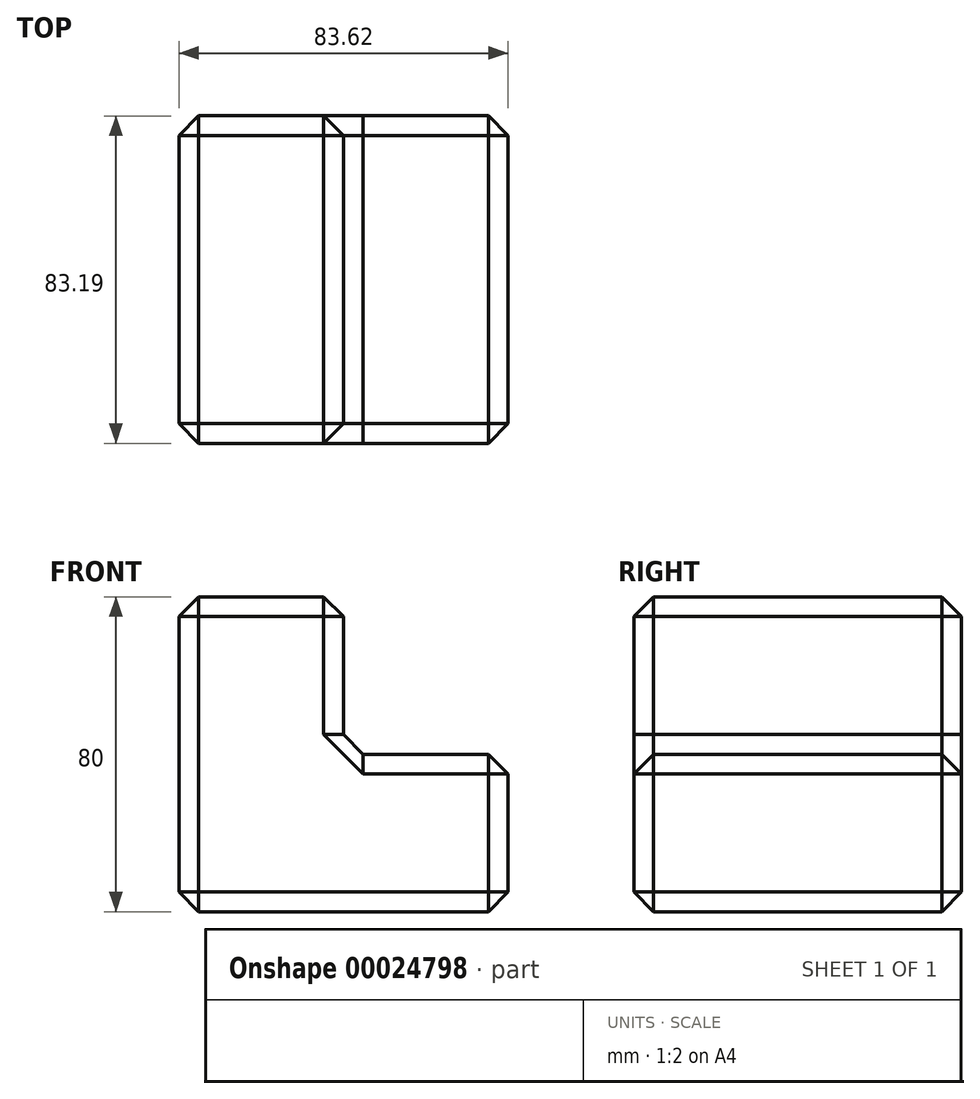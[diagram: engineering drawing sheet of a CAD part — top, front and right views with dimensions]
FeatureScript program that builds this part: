
annotation { "Feature Type Name" : "Feature", "Feature Type Description" : "" }
export const myFeature = defineFeature(function(context is Context, id is Id, definition is map)
    precondition{}
    {
        {
            var Q0;
            Q0=qCreatedBy(makeId("Top.planeOp"),FACE);
            var sketch = newSketch(context, id + "F0", { "sketchPlane" : qUnion([Q0])});
            skLineSegment(sketch, "E0.bottom", {"start": v(-59.13, -45.93) * mm, "end": v(24.5, -45.93) * mm});
            skLineSegment(sketch, "E0.top", {"start": v(-59.13, 37.26) * mm, "end": v(24.5, 37.26) * mm});
            skLineSegment(sketch, "E0.left", {"start": v(-59.13, -45.93) * mm, "end": v(-59.13, 37.26) * mm});
            skLineSegment(sketch, "E0.right", {"start": v(24.5, -45.93) * mm, "end": v(24.5, 37.26) * mm});
            skSolve(sketch);
        }
        {
            var Q0;
            Q0=makeQuery(id+"F0.imprint","IMPRINT",FACE,{"disambiguationData":[TD([[makeQuery(id+"F0.imprint","IMPRINT",EDGE,{"derivedFrom":sQuery(id+"F0.wireOp",EDGE,"E0.bottom")}),1.0]])]});
            extrude(context, id + "F1", {"entities" : qUnion([Q0]), "depth" : 40 * mm});
        }
        {
            var Q0;
            Q0=makeQuery(id+"F1.opExtrude","CAP_FACE",FACE,{"disambiguationData":[OSD([sQuery(id+"F0.wireOp",EDGE,"E0.bottom"),sQuery(id+"F0.wireOp",EDGE,"E0.top"),sQuery(id+"F0.wireOp",EDGE,"E0.left"),sQuery(id+"F0.wireOp",EDGE,"E0.right")])],"isStart":false});
            var sketch = newSketch(context, id + "F2", { "sketchPlane" : qUnion([Q0])});
            skLineSegment(sketch, "E1", {"start": v(-17.32, 37.26) * mm, "end": v(-17.32, -45.93) * mm});
            skSolve(sketch);
        }
        {
            var Q0;
            {var subQ1=sQuery(id+"F2.wireOp",EDGE,"E1");Q0=makeQuery(id+"F2.imprint","IMPRINT",FACE,{"disambiguationData":[TD([[makeQuery(id+"F2.imprint","IMPRINT",EDGE,{"derivedFrom":subQ1}),-1.0]])]});}
            extrude(context, id + "F3", {"entities" : qUnion([Q0]), "operationType" : NewBodyOperationType.ADD, "depth" : 40 * mm});
        }
        {
            var Q0;
            Q0=makeQuery(id+"F3.opExtrude","CAP_FACE",FACE,{"disambiguationData":[OSD([sQuery(id+"F0.wireOp",EDGE,"E0.bottom"),sQuery(id+"F0.wireOp",EDGE,"E0.top"),sQuery(id+"F0.wireOp",EDGE,"E0.left"),sQuery(id+"F2.wireOp",EDGE,"E1")])],"isStart":false});
            var Q1;
            Q1=makeQuery(id+"F3.opExtrude","SWEPT_FACE",FACE,{"disambiguationData":[OSD([sQuery(id+"F2.wireOp",EDGE,"E1")])]});
            var Q2;
            Q2=makeQuery(id+"F1.opExtrude","CAP_FACE",FACE,{"disambiguationData":[OSD([sQuery(id+"F0.wireOp",EDGE,"E0.bottom"),sQuery(id+"F0.wireOp",EDGE,"E0.top"),sQuery(id+"F0.wireOp",EDGE,"E0.left"),sQuery(id+"F0.wireOp",EDGE,"E0.right")])],"isStart":false});
            var Q3;
            Q3=makeQuery(id+"F1.opExtrude","SWEPT_FACE",FACE,{"disambiguationData":[OSD([sQuery(id+"F0.wireOp",EDGE,"E0.right")])]});
            var Q4;
            Q4=makeQuery(id+"F1.opExtrude","CAP_EDGE",EDGE,{"disambiguationData":[OSD([sQuery(id+"F0.wireOp",EDGE,"E0.top")])],"isStart":true});
            var Q5;
            Q5=makeQuery(id+"F1.opExtrude","CAP_FACE",FACE,{"disambiguationData":[OSD([sQuery(id+"F0.wireOp",EDGE,"E0.bottom"),sQuery(id+"F0.wireOp",EDGE,"E0.top"),sQuery(id+"F0.wireOp",EDGE,"E0.left"),sQuery(id+"F0.wireOp",EDGE,"E0.right")])],"isStart":true});
            var Q6;
            {var subQ0=sQuery(id+"F0.wireOp",EDGE,"E0.left");Q6=makeQuery(id+"F3.boolean.opBoolean","MERGE",FACE,{"derivedFrom":[makeQuery(id+"F1.opExtrude","SWEPT_FACE",FACE,{"disambiguationData":[OSD([subQ0])]}),makeQuery(id+"F3.opExtrude","SWEPT_FACE",FACE,{"disambiguationData":[OSD([subQ0])]})]});}
            var Q7;
            {var subQ0=sQuery(id+"F0.wireOp",EDGE,"E0.top");Q7=makeQuery(id+"F3.boolean.opBoolean","MERGE",FACE,{"derivedFrom":[makeQuery(id+"F1.opExtrude","SWEPT_FACE",FACE,{"disambiguationData":[OSD([subQ0])]}),makeQuery(id+"F3.opExtrude","SWEPT_FACE",FACE,{"disambiguationData":[OSD([subQ0])]})]});}
            chamfer(context, id + "F4", {"entities" : qUnion([Q0, Q1, Q2, Q3, Q4, Q5, Q6, Q7]), "width" : 5 * mm, "tangentPropagation" : true});
        }
    });
